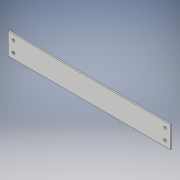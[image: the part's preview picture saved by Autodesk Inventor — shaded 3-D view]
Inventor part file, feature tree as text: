
AUTODESK INVENTOR PART (.ipt)
format: ipt  version: 2017 (Build 210142000, 142)  size: 104,448 bytes
history: native  units: in
note: dims shown in document units (in); Inventor stores cm internally (conversion verified against a paired STEP export)
features: extrude x1, sketch x1
ambient origin geometry x8: Origin, YZ Plane, XZ Plane, XY Plane, X Axis, Y Axis, Z Axis, Center Point
bodies: Solid1 (feature_tree)
feature tree (2):
  extrude  "Extrusion1"  Depth=2.0in
  sketch  "Sketch1"  dims[d0=15.0in d1=2.0in d2=0.5in d3=0.5in d4=1.0in d5=0.25in d6=0.25in d7=0.125in d8=0.0in]
